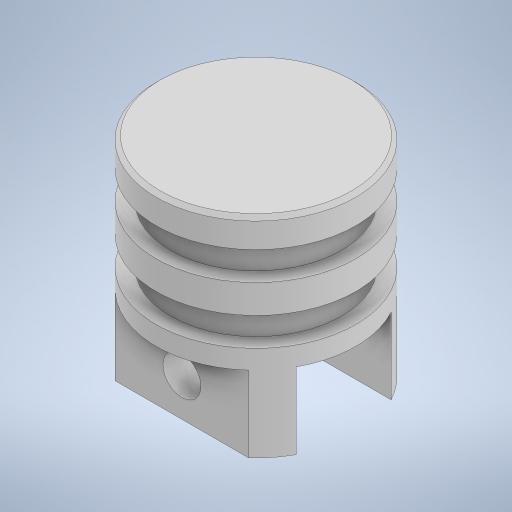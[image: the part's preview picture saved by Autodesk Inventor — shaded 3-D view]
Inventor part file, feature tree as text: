
AUTODESK INVENTOR PART (.ipt)
format: ipt  version: 2023 (Build 270158000, 158)  size: 286,208 bytes
history: native  units: in
note: dims shown in document units (in); Inventor stores cm internally (conversion verified against a paired STEP export)
features: sketch x3, extrude x2, revolve x1, chamfer x1
ambient origin geometry x8: Origin, YZ Plane, XZ Plane, XY Plane, X Axis, Y Axis, Z Axis, Center Point
bodies: Body1 (feature_tree)
feature tree (7):
  revolve  "Revolution1"  [1 undecoded]
  sketch  "Sketch6"  dims[d14=0.6562in]
  chamfer  "Chamfer1"  Distance=0.1875in
  extrude  "Extrusion1"  Depth=0.1875in
  extrude  "Extrusion2"  Depth=0.1875in
  sketch  "Sketch5"  dims[d11=0.75in d12=0.625in]
  sketch  "Sketch7"  dims[d15=0.0938in d16=0.1875in d17=0.1875in d18=0.1875in d19=0.1875in d20=90.0deg d24=0.025in d25=0.125in d26=45.0deg d29=0.5in d30=0.0in d31=0.5in d32=0.0in d33=0.25in d34=1.25in d35=0.0in]
note: 1 required parameter value undecoded (feature->parameter linkage not recoverable at this tier; creation-order binding heuristic only, values carry confidence <= 0.55)
